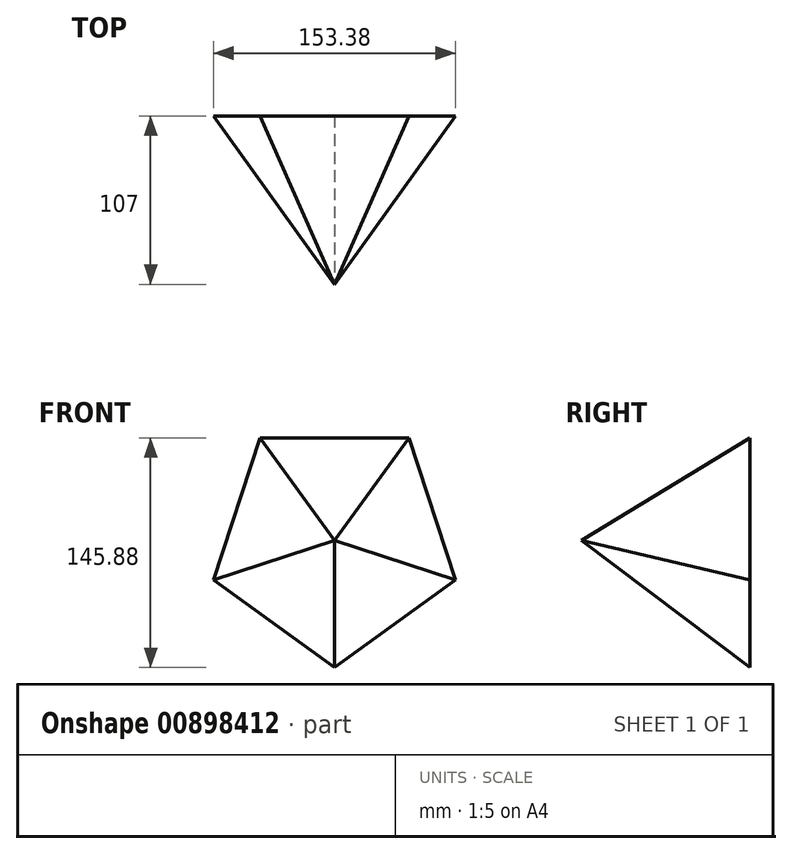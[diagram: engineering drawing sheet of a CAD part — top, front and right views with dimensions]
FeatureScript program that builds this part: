
annotation { "Feature Type Name" : "Feature", "Feature Type Description" : "" }
export const myFeature = defineFeature(function(context is Context, id is Id, definition is map)
    precondition{}
    {
        {
            var Q0;
            Q0=qCreatedBy(makeId("Front.planeOp"),FACE);
            var sketch = newSketch(context, id + "F0", { "sketchPlane" : qUnion([Q0])});
            skCircle(sketch, "E0.cCircle", {"center": v(0, 0) * mm, "radius": 65.24 * mm, "construction": true});
            skLineSegment(sketch, "E0.0", {"start": v(-47.4, 65.24) * mm, "end": v(47.4, 65.24) * mm});
            skLineSegment(sketch, "E0.1", {"start": v(47.4, 65.24) * mm, "end": v(76.7, -24.92) * mm});
            skLineSegment(sketch, "E0.2", {"start": v(76.7, -24.92) * mm, "end": v(0, -80.64) * mm});
            skLineSegment(sketch, "E0.3", {"start": v(0, -80.64) * mm, "end": v(-76.7, -24.92) * mm});
            skLineSegment(sketch, "E0.4", {"start": v(-76.7, -24.92) * mm, "end": v(-47.4, 65.24) * mm});
            skPoint(sketch, "E0.0.midPoint", {"position": v(0, 65.24) * mm});
            skSolve(sketch);
        }
        {
            var Q0;
            Q0=qCreatedBy(makeId("Front.planeOp"),FACE);
            cPlane(context, id + "F1", {"entities" : qUnion([Q0]), "cplaneType" : CPlaneType.OFFSET, "offset" : 107 * mm, "width" : 150 * mm, "height" : 150 * mm});
        }
        {
            var Q0;
            Q0=qCreatedBy(id+"F1.planeOp",FACE);
            var sketch = newSketch(context, id + "F2", { "sketchPlane" : qUnion([Q0])});
            skPoint(sketch, "E1", {"position": v(0, 0) * mm});
            skSolve(sketch);
        }
        {
            var Q0;
            Q0=makeQuery(id+"F0.imprint","IMPRINT",FACE,{"disambiguationData":[TD([[makeQuery(id+"F0.imprint","IMPRINT",EDGE,{"derivedFrom":sQuery(id+"F0.wireOp",EDGE,"E0.0")}),-1.0]])]});
            var Q1;
            Q1=sQuery(id+"F2.wireOp",VERTEX,"E1");
            loft(context, id + "F3", {"sheetProfilesArray" : [{ "sheetProfileEntities" : qUnion([Q0]) }, { "sheetProfileEntities" : qUnion([Q1]) }]});
        }
    });
